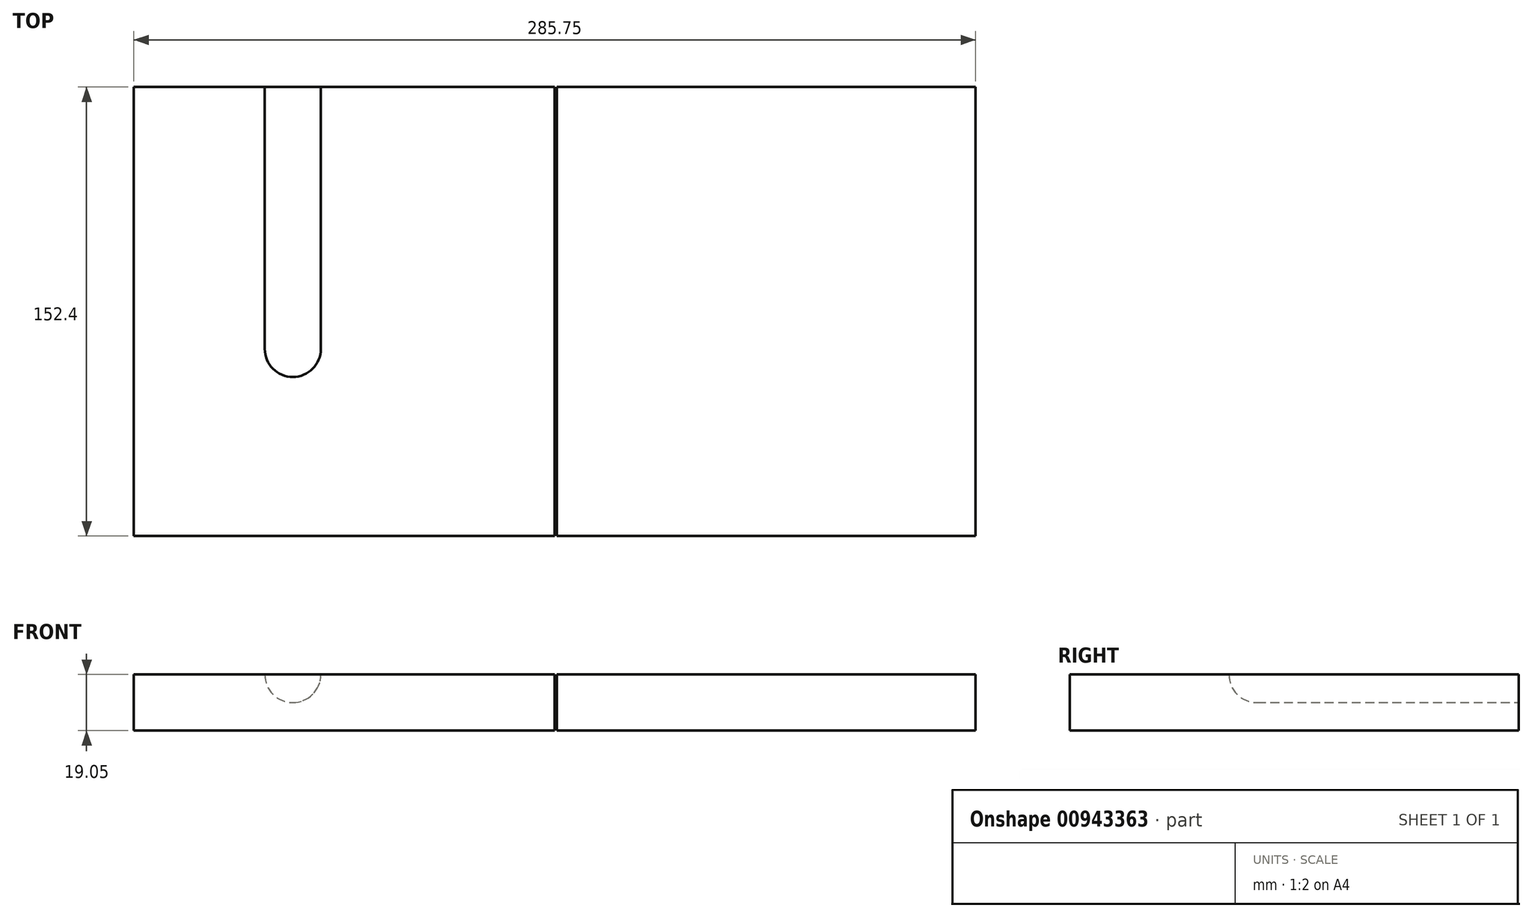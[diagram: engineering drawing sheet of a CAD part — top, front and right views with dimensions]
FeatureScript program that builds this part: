
annotation { "Feature Type Name" : "Feature", "Feature Type Description" : "" }
export const myFeature = defineFeature(function(context is Context, id is Id, definition is map)
    precondition{}
    {
        {
            var Q0;
            Q0=qCreatedBy(makeId("Top.planeOp"),FACE);
            var sketch = newSketch(context, id + "F0", { "sketchPlane" : qUnion([Q0])});
            skLineSegment(sketch, "E0.bottom", {"start": v(-141.52, 17.98) * mm, "end": v(144.23, 17.98) * mm});
            skLineSegment(sketch, "E0.top", {"start": v(-141.52, -134.42) * mm, "end": v(144.23, -134.42) * mm});
            skLineSegment(sketch, "E0.left", {"start": v(-141.52, 17.98) * mm, "end": v(-141.52, -134.42) * mm});
            skLineSegment(sketch, "E0.right", {"start": v(144.23, 17.98) * mm, "end": v(144.23, -134.42) * mm});
            skSolve(sketch);
        }
        {
            var Q0;
            Q0 = qSketchRegion(id + "F0", true);
            extrude(context, id + "F1", {"entities" : qUnion([Q0]), "depth" : 19.05 * mm, "offsetDistance" : 25.4 * mm});
        }
        {
            var Q0;
            Q0=makeQuery(id+"F1.opExtrude","CAP_FACE",FACE,{"disambiguationData":[OSD([sQuery(id+"F0.wireOp",EDGE,"E0.bottom"),sQuery(id+"F0.wireOp",EDGE,"E0.top"),sQuery(id+"F0.wireOp",EDGE,"E0.left"),sQuery(id+"F0.wireOp",EDGE,"E0.right")])],"isStart":false});
            var sketch = newSketch(context, id + "F2", { "sketchPlane" : qUnion([Q0])});
            skLineSegment(sketch, "E1", {"start": v(-97.07, 17.98) * mm, "end": v(-97.07, -70.92) * mm});
            skLineSegment(sketch, "E2", {"start": v(-87.55, -80.44) * mm, "end": v(-87.55, -80.44) * mm});
            skLineSegment(sketch, "E3", {"start": v(-78.02, -70.92) * mm, "end": v(-78.02, 17.98) * mm});
            skLineSegment(sketch, "E4", {"start": v(-97.07, 17.98) * mm, "end": v(-78.02, 17.98) * mm});
            skPoint(sketch, "E5.visualSharp", {"position": v(-97.07, -80.44) * mm});
            skArc(sketch, "E5.filletArc", {"start": v(-97.07, -70.92) * mm, "mid": v(-94.28, -77.65) * mm, "end": v(-87.55, -80.44) * mm});
            skPoint(sketch, "E6.visualSharp", {"position": v(-78.02, -80.44) * mm});
            skArc(sketch, "E6.filletArc", {"start": v(-87.55, -80.44) * mm, "mid": v(-80.81, -77.65) * mm, "end": v(-78.02, -70.92) * mm});
            skLineSegment(sketch, "E7", {"start": v(-141.52, 17.98) * mm, "end": v(144.23, 17.98) * mm});
            skPoint(sketch, "E8.1.0.0", {"position": v(-33.57, -80.44) * mm});
            skLineSegment(sketch, "E8.1.0.1", {"start": v(-52.62, 17.98) * mm, "end": v(-33.57, 17.98) * mm});
            skArc(sketch, "E8.1.0.2", {"start": v(-52.62, -70.92) * mm, "mid": v(-49.83, -77.65) * mm, "end": v(-43.1, -80.44) * mm});
            skPoint(sketch, "E8.1.0.3", {"position": v(-52.62, -80.44) * mm});
            skLineSegment(sketch, "E8.1.0.4", {"start": v(-33.57, -70.92) * mm, "end": v(-33.57, 17.98) * mm});
            skLineSegment(sketch, "E8.1.0.5", {"start": v(-52.62, 17.98) * mm, "end": v(-52.62, -70.92) * mm});
            skArc(sketch, "E8.1.0.6", {"start": v(-43.1, -80.44) * mm, "mid": v(-36.36, -77.65) * mm, "end": v(-33.57, -70.92) * mm});
            skPoint(sketch, "E8.2.0.0", {"position": v(10.88, -80.44) * mm});
            skLineSegment(sketch, "E8.2.0.1", {"start": v(-8.17, 17.98) * mm, "end": v(10.88, 17.98) * mm});
            skArc(sketch, "E8.2.0.2", {"start": v(-8.17, -70.92) * mm, "mid": v(-5.38, -77.65) * mm, "end": v(1.35, -80.44) * mm});
            skPoint(sketch, "E8.2.0.3", {"position": v(-8.17, -80.44) * mm});
            skLineSegment(sketch, "E8.2.0.4", {"start": v(10.88, -70.92) * mm, "end": v(10.88, 17.98) * mm});
            skLineSegment(sketch, "E8.2.0.5", {"start": v(-8.17, 17.98) * mm, "end": v(-8.17, -70.92) * mm});
            skArc(sketch, "E8.2.0.6", {"start": v(1.35, -80.44) * mm, "mid": v(8.09, -77.65) * mm, "end": v(10.88, -70.92) * mm});
            skPoint(sketch, "E8.3.0.0", {"position": v(55.33, -80.44) * mm});
            skLineSegment(sketch, "E8.3.0.1", {"start": v(36.28, 17.98) * mm, "end": v(55.33, 17.98) * mm});
            skArc(sketch, "E8.3.0.2", {"start": v(36.28, -70.92) * mm, "mid": v(39.07, -77.65) * mm, "end": v(45.8, -80.44) * mm});
            skPoint(sketch, "E8.3.0.3", {"position": v(36.28, -80.44) * mm});
            skLineSegment(sketch, "E8.3.0.4", {"start": v(55.33, -70.92) * mm, "end": v(55.33, 17.98) * mm});
            skLineSegment(sketch, "E8.3.0.5", {"start": v(36.28, 17.98) * mm, "end": v(36.28, -70.92) * mm});
            skArc(sketch, "E8.3.0.6", {"start": v(45.8, -80.44) * mm, "mid": v(52.54, -77.65) * mm, "end": v(55.33, -70.92) * mm});
            skPoint(sketch, "E8.4.0.0", {"position": v(99.78, -80.44) * mm});
            skLineSegment(sketch, "E8.4.0.1", {"start": v(80.73, 17.98) * mm, "end": v(99.78, 17.98) * mm});
            skArc(sketch, "E8.4.0.2", {"start": v(80.73, -70.92) * mm, "mid": v(83.52, -77.65) * mm, "end": v(90.25, -80.44) * mm});
            skPoint(sketch, "E8.4.0.3", {"position": v(80.73, -80.44) * mm});
            skLineSegment(sketch, "E8.4.0.4", {"start": v(99.78, -70.92) * mm, "end": v(99.78, 17.98) * mm});
            skLineSegment(sketch, "E8.4.0.5", {"start": v(80.73, 17.98) * mm, "end": v(80.73, -70.92) * mm});
            skArc(sketch, "E8.4.0.6", {"start": v(90.25, -80.44) * mm, "mid": v(96.99, -77.65) * mm, "end": v(99.78, -70.92) * mm});
            skLineSegment(sketch, "E8.direction1", {"start": v(-97.07, -80.44) * mm, "end": v(-52.62, -80.44) * mm, "construction": true});
            skSolve(sketch);
        }
        {
            var Q0;
            {var subQ1=sQuery(id+"F2.wireOp",EDGE,"E1");Q0=makeQuery(id+"F2.imprint","IMPRINT",FACE,{"disambiguationData":[TD([[makeQuery(id+"F2.imprint","IMPRINT",EDGE,{"derivedFrom":subQ1}),1.0]])]});}
            var Q1;
            Q1=makeQuery(id+"F2.imprint","IMPRINT",FACE,{"disambiguationData":[TD([[makeQuery(id+"F2.imprint","IMPRINT",EDGE,{"derivedFrom":sQuery(id+"F2.wireOp",EDGE,"E8.1.0.1")}),-1.0]])]});
            var Q2;
            Q2=makeQuery(id+"F2.imprint","IMPRINT",FACE,{"disambiguationData":[TD([[makeQuery(id+"F2.imprint","IMPRINT",EDGE,{"derivedFrom":sQuery(id+"F2.wireOp",EDGE,"E8.2.0.1")}),-1.0]])]});
            var Q3;
            Q3=makeQuery(id+"F2.imprint","IMPRINT",FACE,{"disambiguationData":[TD([[makeQuery(id+"F2.imprint","IMPRINT",EDGE,{"derivedFrom":sQuery(id+"F2.wireOp",EDGE,"E8.3.0.1")}),-1.0]])]});
            var Q4;
            Q4=makeQuery(id+"F2.imprint","IMPRINT",FACE,{"disambiguationData":[TD([[makeQuery(id+"F2.imprint","IMPRINT",EDGE,{"derivedFrom":sQuery(id+"F2.wireOp",EDGE,"E8.4.0.1")}),-1.0]])]});
            extrude(context, id + "F3", {"entities" : qUnion([Q0, Q1, Q2, Q3, Q4]), "operationType" : NewBodyOperationType.REMOVE, "oppositeDirection" : true, "depth" : 9.52 * mm, "offsetDistance" : 25.4 * mm});
        }
        {
            var Q0;
            Q0=makeQuery(id+"F3.boolean.opBoolean","COPY",EDGE,{"derivedFrom":makeQuery(id+"F3.opExtrude","CAP_EDGE",EDGE,{"disambiguationData":[OSD([sQuery(id+"F2.wireOp",EDGE,"E5.filletArc"),sQuery(id+"F2.wireOp",EDGE,"E6.filletArc")])],"isStart":false})});
            var Q1;
            Q1=makeQuery(id+"F3.boolean.opBoolean","COPY",EDGE,{"derivedFrom":makeQuery(id+"F3.opExtrude","CAP_EDGE",EDGE,{"disambiguationData":[OSD([sQuery(id+"F2.wireOp",EDGE,"E8.1.0.5")])],"isStart":false})});
            var Q2;
            Q2=makeQuery(id+"F3.boolean.opBoolean","COPY",EDGE,{"derivedFrom":makeQuery(id+"F3.opExtrude","CAP_EDGE",EDGE,{"disambiguationData":[OSD([sQuery(id+"F2.wireOp",EDGE,"E8.2.0.5")])],"isStart":false})});
            var Q3;
            Q3=makeQuery(id+"F3.boolean.opBoolean","COPY",EDGE,{"derivedFrom":makeQuery(id+"F3.opExtrude","CAP_EDGE",EDGE,{"disambiguationData":[OSD([sQuery(id+"F2.wireOp",EDGE,"E8.3.0.5")])],"isStart":false})});
            var Q4;
            Q4=makeQuery(id+"F3.boolean.opBoolean","COPY",EDGE,{"derivedFrom":makeQuery(id+"F3.opExtrude","CAP_EDGE",EDGE,{"disambiguationData":[OSD([sQuery(id+"F2.wireOp",EDGE,"E8.4.0.5")])],"isStart":false})});
            fillet(context, id + "F4", {"entities" : qUnion([Q0, Q1, Q2, Q3, Q4]), "radius" : 9.52 * mm, "tangentPropagation" : true, "allowEdgeOverflow" : false});
        }
        {
            var Q0;
            Q0=makeQuery(id+"F1.opExtrude","CAP_FACE",FACE,{"disambiguationData":[OSD([sQuery(id+"F0.wireOp",EDGE,"E0.bottom"),sQuery(id+"F0.wireOp",EDGE,"E0.top"),sQuery(id+"F0.wireOp",EDGE,"E0.left"),sQuery(id+"F0.wireOp",EDGE,"E0.right")])],"isStart":false});
            var sketch = newSketch(context, id + "F5", { "sketchPlane" : qUnion([Q0])});
            skLineSegment(sketch, "E9", {"start": v(1.35, -134.42) * mm, "end": v(1.35, 17.98) * mm});
            skLineSegment(sketch, "E10", {"start": v(1.35, 17.98) * mm, "end": v(2.15, 17.98) * mm});
            skLineSegment(sketch, "E11", {"start": v(2.15, 17.98) * mm, "end": v(2.15, -134.42) * mm});
            skLineSegment(sketch, "E12", {"start": v(1.35, -134.42) * mm, "end": v(2.15, -134.42) * mm});
            skSolve(sketch);
        }
        {
            var Q0;
            {var subQ0=sQuery(id+"F5.wireOp",EDGE,"E10");Q0=makeQuery(id+"F5.imprint","IMPRINT",FACE,{"disambiguationData":[TD([[makeQuery(id+"F5.imprint","IMPRINT",EDGE,{"derivedFrom":subQ0}),-1.0]])]});}
            var Q1;
            {var subQ0=sQuery(id+"F5.wireOp",EDGE,"E12");Q1=makeQuery(id+"F5.imprint","IMPRINT",FACE,{"disambiguationData":[TD([[makeQuery(id+"F5.imprint","IMPRINT",EDGE,{"derivedFrom":subQ0}),1.0]])]});}
            extrude(context, id + "F6", {"entities" : qUnion([Q0, Q1]), "operationType" : NewBodyOperationType.REMOVE, "oppositeDirection" : true, "depth" : 25.4 * mm, "offsetDistance" : 25.4 * mm});
        }
    });
